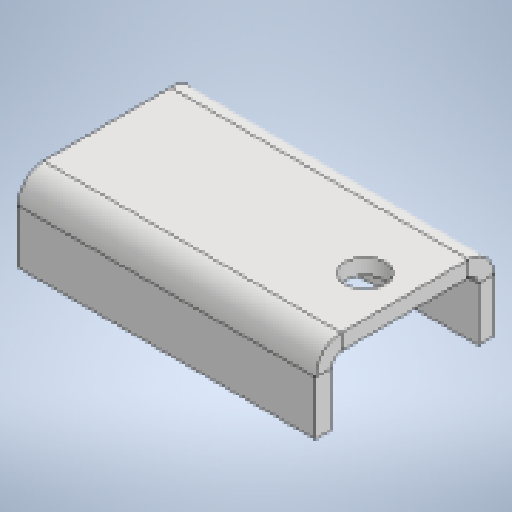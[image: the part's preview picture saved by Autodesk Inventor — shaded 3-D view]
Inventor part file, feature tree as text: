
AUTODESK INVENTOR PART (.ipt)
format: ipt  version: 2025.1 (Build 291241020, 241B)  size: 190,976 bytes
history: native  units: mm
features: sheet_metal_op x4, other x3, sketch x2
ambient origin geometry x8: Origin, YZ Plane, XZ Plane, XY Plane, X Axis, Y Axis, Z Axis, Center Point
bodies: Solid1 (feature_tree)
feature tree (9):
  sheet_metal_op  "Face1"
  sheet_metal_op  "Flange2"
  sketch  "Sketch1"  dims[d0=150.0mm]
  other  "Plate1"
  sketch  "Sketch6"  dims[d1=90.0mm d2=8.0mm d23=20.0mm d25=20.0mm d26=20.0mm d30=8.0mm d31=4.0mm d32=16.0mm d33=5.0mm d34=40.0mm d35=90.0deg d36=5.0mm d37=32.0mm d38=8.0mm d39=5.0mm]
  other  "Plate3"
  sheet_metal_op  "Bend2"
  sheet_metal_op  "Corner2"
  other  "Definition1"
